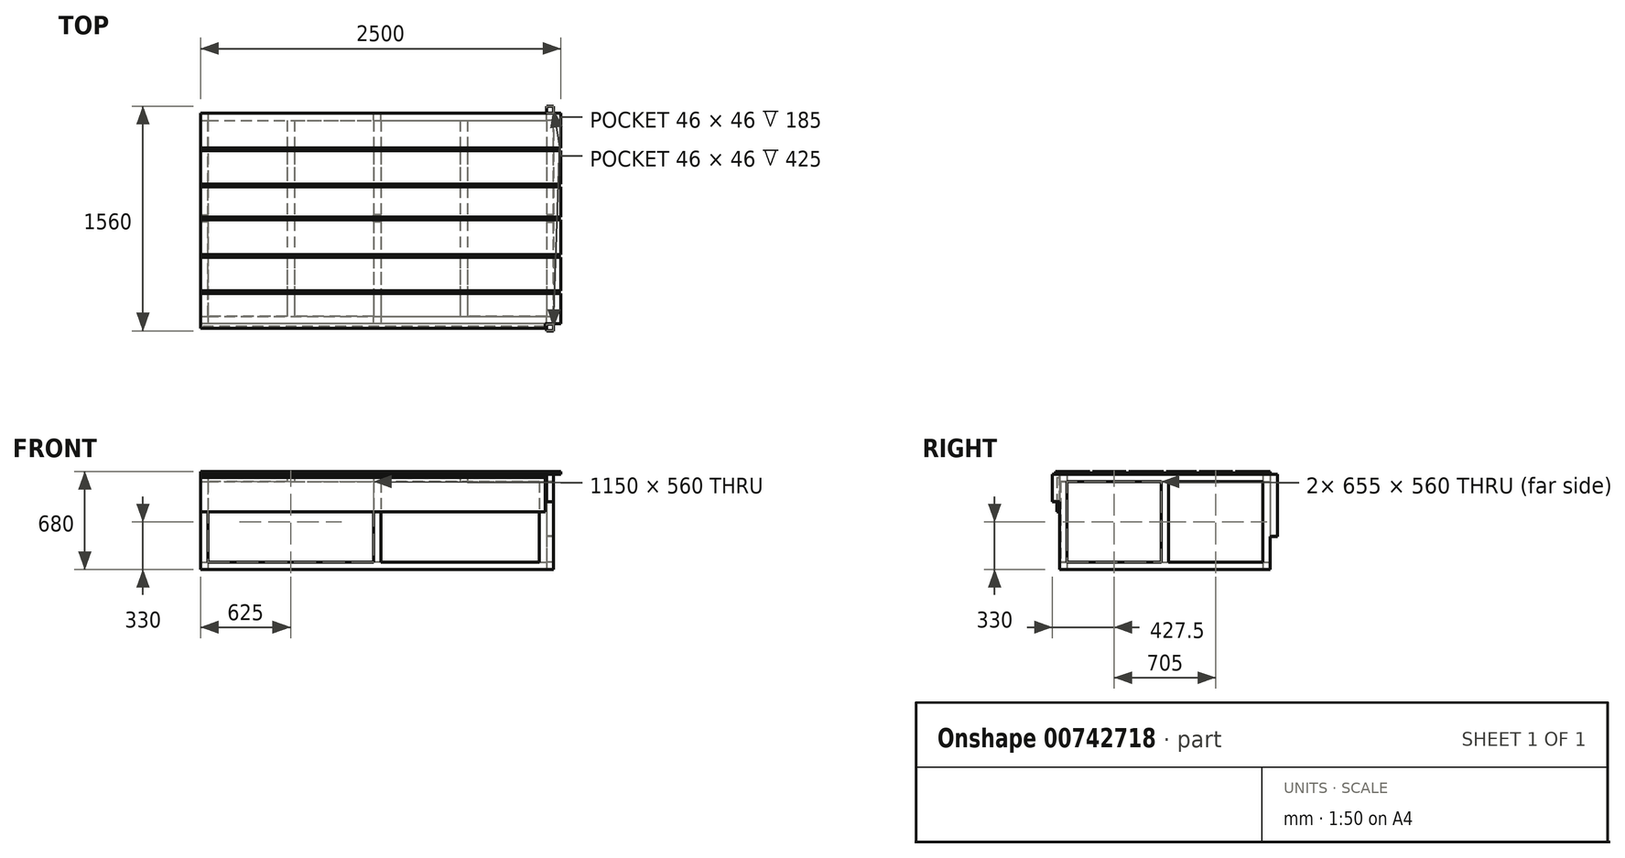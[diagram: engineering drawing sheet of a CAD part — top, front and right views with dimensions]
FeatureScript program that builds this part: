
annotation { "Feature Type Name" : "Feature", "Feature Type Description" : "" }
export const myFeature = defineFeature(function(context is Context, id is Id, definition is map)
    precondition{}
    {
        {
            var Q0;
            Q0=qCreatedBy(makeId("Top.planeOp"),FACE);
            var sketch = newSketch(context, id + "F0", { "sketchPlane" : qUnion([Q0])});
            skLineSegment(sketch, "E0.bottom", {"start": v(1225, -730) * mm, "end": v(-1225, -730) * mm});
            skLineSegment(sketch, "E0.top", {"start": v(1225, 730) * mm, "end": v(-1225, 730) * mm});
            skLineSegment(sketch, "E0.left", {"start": v(1225, -730) * mm, "end": v(1225, 730) * mm});
            skLineSegment(sketch, "E0.right", {"start": v(-1225, -730) * mm, "end": v(-1225, 730) * mm});
            skPoint(sketch, "E0.middle", {"position": v(0, 0) * mm});
            skLineSegment(sketch, "E1.bottom", {"start": v(-1175, 680) * mm, "end": v(1175, 680) * mm});
            skLineSegment(sketch, "E1.top", {"start": v(-1175, -680) * mm, "end": v(1175, -680) * mm});
            skLineSegment(sketch, "E1.left", {"start": v(-1175, 680) * mm, "end": v(-1175, -680) * mm});
            skLineSegment(sketch, "E1.right", {"start": v(1175, 680) * mm, "end": v(1175, -680) * mm});
            skLineSegment(sketch, "E2.bottom", {"start": v(25, 680) * mm, "end": v(-25, 680) * mm});
            skLineSegment(sketch, "E2.top", {"start": v(25, -680) * mm, "end": v(-25, -680) * mm});
            skLineSegment(sketch, "E2.left", {"start": v(25, 680) * mm, "end": v(25, -680) * mm});
            skLineSegment(sketch, "E2.right", {"start": v(-25, 680) * mm, "end": v(-25, -680) * mm});
            skSolve(sketch);
        }
        {
            var Q0;
            Q0=qSketchRegion(id+"F0",true);
            var Q1;
            Q1=makeQuery(id+"F0.imprint","IMPRINT",FACE,{"disambiguationData":[TD([[makeQuery(id+"F0.imprint","IMPRINT",EDGE,{"derivedFrom":sQuery(id+"F0.wireOp",EDGE,"E2.bottom")}),1.0]])]});
            extrude(context, id + "F1", {"entities" : qUnion([Q0, Q1]), "depth" : 50 * mm, "offsetDistance" : 25 * mm});
        }
        {
            var Q0;
            Q0=makeQuery(id+"F1.opExtrude","CAP_FACE",FACE,{"disambiguationData":[OSD([sQuery(id+"F0.wireOp",EDGE,"E0.bottom"),sQuery(id+"F0.wireOp",EDGE,"E0.top"),sQuery(id+"F0.wireOp",EDGE,"E0.left"),sQuery(id+"F0.wireOp",EDGE,"E0.right"),sQuery(id+"F0.wireOp",EDGE,"E1.bottom"),sQuery(id+"F0.wireOp",EDGE,"E1.top"),sQuery(id+"F0.wireOp",EDGE,"E1.left"),sQuery(id+"F0.wireOp",EDGE,"E1.right"),sQuery(id+"F0.wireOp",EDGE,"E2.left"),sQuery(id+"F0.wireOp",EDGE,"E2.right")])],"isStart":false});
            var sketch = newSketch(context, id + "F2", { "sketchPlane" : qUnion([Q0])});
            skLineSegment(sketch, "E3.bottom", {"start": v(-1225, 730) * mm, "end": v(-1175, 730) * mm});
            skLineSegment(sketch, "E3.top", {"start": v(-1225, 680) * mm, "end": v(-1175, 680) * mm});
            skLineSegment(sketch, "E3.left", {"start": v(-1225, 730) * mm, "end": v(-1225, 680) * mm});
            skLineSegment(sketch, "E3.right", {"start": v(-1175, 730) * mm, "end": v(-1175, 680) * mm});
            skLineSegment(sketch, "E4", {"start": v(-25, 680) * mm, "end": v(-25, 730) * mm});
            skLineSegment(sketch, "E5", {"start": v(25, 680) * mm, "end": v(25, 730) * mm});
            skLineSegment(sketch, "E6", {"start": v(25, 730) * mm, "end": v(-25, 730) * mm});
            skLineSegment(sketch, "E7", {"start": v(-25, 680) * mm, "end": v(25, 680) * mm});
            skLineSegment(sketch, "E8", {"start": v(1175, 680) * mm, "end": v(1175, 730) * mm});
            skLineSegment(sketch, "E9", {"start": v(1175, 730) * mm, "end": v(1225, 730) * mm});
            skLineSegment(sketch, "E10", {"start": v(1225, 730) * mm, "end": v(1225, 680) * mm});
            skLineSegment(sketch, "E11", {"start": v(1225, 680) * mm, "end": v(1175, 680) * mm});
            skLineSegment(sketch, "E12", {"start": v(1175, -680) * mm, "end": v(1225, -680) * mm});
            skLineSegment(sketch, "E13", {"start": v(1225, -680) * mm, "end": v(1225, -730) * mm});
            skLineSegment(sketch, "E14", {"start": v(1225, -730) * mm, "end": v(1175, -730) * mm});
            skLineSegment(sketch, "E15", {"start": v(1175, -730) * mm, "end": v(1175, -680) * mm});
            skLineSegment(sketch, "E16", {"start": v(-25, -680) * mm, "end": v(25, -680) * mm});
            skLineSegment(sketch, "E17", {"start": v(25, -680) * mm, "end": v(25, -730) * mm});
            skLineSegment(sketch, "E18", {"start": v(25, -730) * mm, "end": v(-25, -730) * mm});
            skLineSegment(sketch, "E19", {"start": v(-25, -730) * mm, "end": v(-25, -680) * mm});
            skLineSegment(sketch, "E20", {"start": v(-1175, -680) * mm, "end": v(-1175, -730) * mm});
            skLineSegment(sketch, "E21", {"start": v(-1175, -730) * mm, "end": v(-1225, -730) * mm});
            skLineSegment(sketch, "E22", {"start": v(-1225, -730) * mm, "end": v(-1225, -680) * mm});
            skLineSegment(sketch, "E23", {"start": v(-1225, -680) * mm, "end": v(-1175, -680) * mm});
            skLineSegment(sketch, "E24.bottom", {"start": v(25, -25) * mm, "end": v(-25, -25) * mm});
            skLineSegment(sketch, "E24.top", {"start": v(25, 25) * mm, "end": v(-25, 25) * mm});
            skLineSegment(sketch, "E24.left", {"start": v(25, -25) * mm, "end": v(25, 25) * mm});
            skLineSegment(sketch, "E24.right", {"start": v(-25, -25) * mm, "end": v(-25, 25) * mm});
            skPoint(sketch, "E24.middle", {"position": v(0, 0) * mm});
            skLineSegment(sketch, "E25", {"start": v(0, 0) * mm, "end": v(-1225, 0) * mm});
            skLineSegment(sketch, "E26", {"start": v(-1225, 25) * mm, "end": v(-1175, 25) * mm});
            skLineSegment(sketch, "E27", {"start": v(-1175, 25) * mm, "end": v(-1175, -25) * mm});
            skLineSegment(sketch, "E28", {"start": v(-1175, -25) * mm, "end": v(-1225, -25) * mm});
            skLineSegment(sketch, "E29", {"start": v(-1225, 25) * mm, "end": v(-1225, -25) * mm});
            skLineSegment(sketch, "E30.MirrorCS", {"start": v(1225, 25) * mm, "end": v(1225, -25) * mm});
            skLineSegment(sketch, "E31.MirrorCS", {"start": v(1175, -25) * mm, "end": v(1225, -25) * mm});
            skLineSegment(sketch, "E32.MirrorCS", {"start": v(1225, 25) * mm, "end": v(1175, 25) * mm});
            skLineSegment(sketch, "E33.MirrorCS", {"start": v(1175, 25) * mm, "end": v(1175, -25) * mm});
            skSolve(sketch);
        }
        {
            var Q0;
            Q0=qSketchRegion(id+"F2",true);
            extrude(context, id + "F3", {"entities" : qUnion([Q0]), "operationType" : NewBodyOperationType.ADD, "depth" : 560 * mm, "offsetDistance" : 25 * mm});
        }
        {
            var Q0;
            Q0=makeQuery(id+"F3.opExtrude","CAP_FACE",FACE,{"disambiguationData":[OSD([sQuery(id+"F2.wireOp",EDGE,"E26"),sQuery(id+"F2.wireOp",EDGE,"E27"),sQuery(id+"F2.wireOp",EDGE,"E28"),sQuery(id+"F2.wireOp",EDGE,"E29")])],"isStart":false});
            var sketch = newSketch(context, id + "F4", { "sketchPlane" : qUnion([Q0])});
            skLineSegment(sketch, "E34", {"start": v(-1225, 25) * mm, "end": v(-1225, 730) * mm});
            skLineSegment(sketch, "E35", {"start": v(-1225, 730) * mm, "end": v(-1175, 730) * mm});
            skLineSegment(sketch, "E36", {"start": v(-1175, 730) * mm, "end": v(1225, 730) * mm});
            skLineSegment(sketch, "E37", {"start": v(1225, 730) * mm, "end": v(1225, -730) * mm});
            skLineSegment(sketch, "E38", {"start": v(1225, -730) * mm, "end": v(-1225, -730) * mm});
            skLineSegment(sketch, "E39", {"start": v(-1225, -730) * mm, "end": v(-1225, 25) * mm});
            skLineSegment(sketch, "E40", {"start": v(-1175, 730) * mm, "end": v(-1175, 680) * mm});
            skLineSegment(sketch, "E41", {"start": v(-1175, 680) * mm, "end": v(-25, 680) * mm});
            skLineSegment(sketch, "E42", {"start": v(-1175, 680) * mm, "end": v(-600, 680) * mm});
            skLineSegment(sketch, "E43", {"start": v(-600, 680) * mm, "end": v(-575, 680) * mm});
            skLineSegment(sketch, "E44", {"start": v(-600, 680) * mm, "end": v(-625, 680) * mm});
            skLineSegment(sketch, "E45", {"start": v(-625, 680) * mm, "end": v(-625, -680) * mm});
            skLineSegment(sketch, "E46.MirrorCS", {"start": v(-575, 680) * mm, "end": v(-575, -680) * mm});
            skLineSegment(sketch, "E47", {"start": v(-25, 680) * mm, "end": v(25, 680) * mm});
            skLineSegment(sketch, "E48", {"start": v(25, 680) * mm, "end": v(1175, 680) * mm});
            skLineSegment(sketch, "E49", {"start": v(25, 680) * mm, "end": v(600, 680) * mm});
            skLineSegment(sketch, "E50", {"start": v(600, 680) * mm, "end": v(575, 680) * mm});
            skLineSegment(sketch, "E51", {"start": v(575, 680) * mm, "end": v(575, -680) * mm});
            skLineSegment(sketch, "E52.MirrorCS", {"start": v(625, 680) * mm, "end": v(625, -680) * mm});
            skLineSegment(sketch, "E53", {"start": v(-25, 680) * mm, "end": v(-25, -680) * mm});
            skLineSegment(sketch, "E54", {"start": v(-25, -680) * mm, "end": v(-575, -680) * mm});
            skLineSegment(sketch, "E55", {"start": v(-625, -680) * mm, "end": v(-1175, -680) * mm});
            skLineSegment(sketch, "E56", {"start": v(-1175, -680) * mm, "end": v(-1175, 680) * mm});
            skLineSegment(sketch, "E57", {"start": v(1175, 680) * mm, "end": v(1175, -680) * mm});
            skLineSegment(sketch, "E58", {"start": v(1175, -680) * mm, "end": v(625, -680) * mm});
            skLineSegment(sketch, "E59", {"start": v(25, 680) * mm, "end": v(25, -680) * mm});
            skLineSegment(sketch, "E60", {"start": v(25, -680) * mm, "end": v(575, -680) * mm});
            skSolve(sketch);
        }
        {
            var Q0;
            Q0=qSketchRegion(id+"F4",true);
            extrude(context, id + "F5", {"entities" : qUnion([Q0]), "operationType" : NewBodyOperationType.ADD, "depth" : 50 * mm, "offsetDistance" : 25 * mm});
        }
        {
            var Q0;
            {var subQ5=sQuery(id+"F0.wireOp",EDGE,"E1.left");var subQ6=sQuery(id+"F0.wireOp",EDGE,"E1.top");var subQ8=makeQuery(id+"F1.opExtrude","CAP_EDGE",EDGE,{"disambiguationData":[OSD([subQ6]),TDD([makeQuery(id+"F0.imprint","IMPRINT",EDGE,{"disambiguationData":[TD([[makeQuery(id+"F0.imprint","INTERSECT",VERTEX,{"derivedFrom":[subQ6,subQ5]}),-1.0]])],"derivedFrom":subQ6})])],"isStart":false});Q0=makeQuery(id+"F2.imprint","IMPRINT",FACE,{"disambiguationData":[TD([[makeQuery(id+"F2.imprint","IMPRINT",EDGE,{"derivedFrom":subQ8}),1.0]])]});}
            cPlane(context, id + "F6", {"entities" : qUnion([Q0]), "cplaneType" : CPlaneType.OFFSET, "offset" : 420 * mm, "width" : 150 * mm, "height" : 150 * mm});
        }
        {
            var Q0;
            {var subQ5=sQuery(id+"F0.wireOp",EDGE,"E1.left");var subQ6=sQuery(id+"F0.wireOp",EDGE,"E1.top");var subQ8=makeQuery(id+"F1.opExtrude","CAP_EDGE",EDGE,{"disambiguationData":[OSD([subQ6]),TDD([makeQuery(id+"F0.imprint","IMPRINT",EDGE,{"disambiguationData":[TD([[makeQuery(id+"F0.imprint","INTERSECT",VERTEX,{"derivedFrom":[subQ6,subQ5]}),-1.0]])],"derivedFrom":subQ6})])],"isStart":false});Q0=makeQuery(id+"F2.imprint","IMPRINT",FACE,{"disambiguationData":[TD([[makeQuery(id+"F2.imprint","IMPRINT",EDGE,{"derivedFrom":subQ8}),1.0]])]});}
            cPlane(context, id + "F7", {"entities" : qUnion([Q0]), "cplaneType" : CPlaneType.OFFSET, "offset" : 180 * mm, "width" : 150 * mm, "height" : 150 * mm});
        }
        {
            var Q0;
            Q0=qCreatedBy(id+"F7.planeOp",FACE);
            var sketch = newSketch(context, id + "F8", { "sketchPlane" : qUnion([Q0])});
            skLineSegment(sketch, "E61.bottom", {"start": v(1225, 730) * mm, "end": v(1175, 730) * mm});
            skLineSegment(sketch, "E61.top", {"start": v(1225, 780) * mm, "end": v(1175, 780) * mm});
            skLineSegment(sketch, "E61.left", {"start": v(1225, 730) * mm, "end": v(1225, 780) * mm});
            skLineSegment(sketch, "E61.right", {"start": v(1175, 730) * mm, "end": v(1175, 780) * mm});
            skSolve(sketch);
        }
        {
            var Q0;
            Q0=qCreatedBy(id+"F6.planeOp",FACE);
            var sketch = newSketch(context, id + "F9", { "sketchPlane" : qUnion([Q0])});
            skLineSegment(sketch, "E62.bottom", {"start": v(1225, -730) * mm, "end": v(1175, -730) * mm});
            skLineSegment(sketch, "E62.top", {"start": v(1225, -780) * mm, "end": v(1175, -780) * mm});
            skLineSegment(sketch, "E62.right", {"start": v(1175, -730) * mm, "end": v(1175, -780) * mm});
            skLineSegment(sketch, "E63", {"start": v(1225, -730) * mm, "end": v(1225, -780) * mm});
            skSolve(sketch);
        }
        {
            var Q0;
            Q0 = qSketchRegion(id + "F9", true);
            extrude(context, id + "F10", {"entities" : qUnion([Q0]), "operationType" : NewBodyOperationType.ADD, "depth" : 5 * mm, "offsetDistance" : 25 * mm});
        }
        {
            var Q0;
            Q0=makeQuery(id+"F10.opExtrude","CAP_FACE",FACE,{"disambiguationData":[OSD([sQuery(id+"F9.wireOp",EDGE,"E62.bottom"),sQuery(id+"F9.wireOp",EDGE,"E62.top"),sQuery(id+"F9.wireOp",EDGE,"E62.right"),sQuery(id+"F9.wireOp",EDGE,"E63")])],"isStart":false});
            var sketch = newSketch(context, id + "F11", { "sketchPlane" : qUnion([Q0])});
            skLineSegment(sketch, "E64", {"start": v(1175, -730) * mm, "end": v(1175, -780) * mm});
            skLineSegment(sketch, "E65", {"start": v(1175, -780) * mm, "end": v(1225, -780) * mm});
            skLineSegment(sketch, "E66", {"start": v(1225, -780) * mm, "end": v(1225, -730) * mm});
            skLineSegment(sketch, "E67", {"start": v(1225, -730) * mm, "end": v(1175, -730) * mm});
            skLineSegment(sketch, "E68", {"start": v(1175, -730) * mm, "end": v(1177, -730) * mm});
            skLineSegment(sketch, "E69", {"start": v(1177, -730) * mm, "end": v(1177, -732) * mm});
            skLineSegment(sketch, "E70.bottom", {"start": v(1177, -732) * mm, "end": v(1223, -732) * mm});
            skLineSegment(sketch, "E70.top", {"start": v(1177, -778) * mm, "end": v(1223, -778) * mm});
            skLineSegment(sketch, "E70.left", {"start": v(1177, -732) * mm, "end": v(1177, -778) * mm});
            skLineSegment(sketch, "E70.right", {"start": v(1223, -732) * mm, "end": v(1223, -778) * mm});
            skSolve(sketch);
        }
        {
            var Q0;
            Q0 = qSketchRegion(id + "F11", true);
            var Q1;
            {var subQ0=sQuery(id+"F4.wireOp",EDGE,"E60");var subQ1=sQuery(id+"F4.wireOp",EDGE,"E59");var subQ2=sQuery(id+"F4.wireOp",EDGE,"E58");var subQ3=sQuery(id+"F4.wireOp",EDGE,"E57");var subQ4=sQuery(id+"F4.wireOp",EDGE,"E56");var subQ5=sQuery(id+"F4.wireOp",EDGE,"E55");var subQ6=sQuery(id+"F4.wireOp",EDGE,"E54");var subQ7=sQuery(id+"F4.wireOp",EDGE,"E53");var subQ8=sQuery(id+"F4.wireOp",EDGE,"E52.MirrorCS");var subQ9=sQuery(id+"F4.wireOp",EDGE,"E51");var subQ10=sQuery(id+"F4.wireOp",EDGE,"E49");var subQ11=sQuery(id+"F4.wireOp",EDGE,"E48");var subQ12=sQuery(id+"F4.wireOp",EDGE,"E46.MirrorCS");var subQ13=sQuery(id+"F4.wireOp",EDGE,"E45");var subQ14=sQuery(id+"F4.wireOp",EDGE,"E42");var subQ15=sQuery(id+"F4.wireOp",EDGE,"E41");var subQ16=sQuery(id+"F4.wireOp",EDGE,"E39");var subQ17=sQuery(id+"F4.wireOp",EDGE,"E38");var subQ18=sQuery(id+"F4.wireOp",EDGE,"E37");var subQ19=sQuery(id+"F4.wireOp",EDGE,"E36");var subQ20=sQuery(id+"F4.wireOp",EDGE,"E35");var subQ21=sQuery(id+"F4.wireOp",EDGE,"E34");Q1=makeQuery(id+"FP4IzDu3Lu8PIDH_1.boolean.opBoolean","MERGE",FACE,{"derivedFrom":[makeQuery(id+"F5.opExtrude","CAP_FACE",FACE,{"disambiguationData":[OSD([subQ21,subQ20,subQ19,subQ18,subQ17,subQ16,subQ15,subQ14,subQ13,subQ12,subQ11,subQ10,subQ9,subQ8,subQ7,subQ6,subQ5,subQ4,subQ3,subQ2,subQ1,subQ0])],"isStart":false}),makeQuery(id+"FP4IzDu3Lu8PIDH_1.opExtrude","CAP_FACE",FACE,{"disambiguationData":[OSD([subQ21,subQ20,subQ19,subQ18,subQ17,subQ16,subQ15,subQ14,subQ13,subQ12,subQ11,subQ10,subQ9,subQ8,subQ7,subQ6,subQ5,subQ4,subQ3,subQ2,subQ1,subQ0])],"isStart":false})]});}
            extrude(context, id + "F12", {"entities" : qUnion([Q0]), "operationType" : NewBodyOperationType.ADD, "endBound" : BoundingType.UP_TO_SURFACE, "depth" : 25 * mm, "endBoundEntityFace" : qUnion([Q1]), "offsetDistance" : 25 * mm});
        }
        {
            var Q0;
            Q0 = qSketchRegion(id + "F8", true);
            extrude(context, id + "F13", {"entities" : qUnion([Q0]), "operationType" : NewBodyOperationType.ADD, "depth" : 5 * mm, "offsetDistance" : 25 * mm});
        }
        {
            var Q0;
            Q0=makeQuery(id+"F13.opExtrude","CAP_FACE",FACE,{"disambiguationData":[OSD([sQuery(id+"F8.wireOp",EDGE,"E61.bottom"),sQuery(id+"F8.wireOp",EDGE,"E61.top"),sQuery(id+"F8.wireOp",EDGE,"E61.left"),sQuery(id+"F8.wireOp",EDGE,"E61.right")])],"isStart":false});
            var sketch = newSketch(context, id + "F14", { "sketchPlane" : qUnion([Q0])});
            skLineSegment(sketch, "E71.bottom", {"start": v(1175, 780) * mm, "end": v(1177, 780) * mm});
            skLineSegment(sketch, "E71.top", {"start": v(1175, 778) * mm, "end": v(1177, 778) * mm});
            skLineSegment(sketch, "E71.left", {"start": v(1175, 780) * mm, "end": v(1175, 778) * mm});
            skLineSegment(sketch, "E71.right", {"start": v(1177, 780) * mm, "end": v(1177, 778) * mm});
            skLineSegment(sketch, "E72.bottom", {"start": v(1177, 778) * mm, "end": v(1223, 778) * mm});
            skLineSegment(sketch, "E72.top", {"start": v(1177, 732) * mm, "end": v(1223, 732) * mm});
            skLineSegment(sketch, "E72.left", {"start": v(1177, 778) * mm, "end": v(1177, 732) * mm});
            skLineSegment(sketch, "E72.right", {"start": v(1223, 778) * mm, "end": v(1223, 732) * mm});
            skLineSegment(sketch, "E73.bottom", {"start": v(1175, 780) * mm, "end": v(1225, 780) * mm});
            skLineSegment(sketch, "E73.top", {"start": v(1175, 730) * mm, "end": v(1225, 730) * mm});
            skLineSegment(sketch, "E73.left", {"start": v(1175, 780) * mm, "end": v(1175, 730) * mm});
            skLineSegment(sketch, "E73.right", {"start": v(1225, 780) * mm, "end": v(1225, 730) * mm});
            skSolve(sketch);
        }
        {
            var Q0;
            Q0 = qSketchRegion(id + "F14", true);
            var Q1;
            {var subQ0=sQuery(id+"F4.wireOp",EDGE,"E60");var subQ1=sQuery(id+"F4.wireOp",EDGE,"E59");var subQ2=sQuery(id+"F4.wireOp",EDGE,"E58");var subQ3=sQuery(id+"F4.wireOp",EDGE,"E57");var subQ4=sQuery(id+"F4.wireOp",EDGE,"E56");var subQ5=sQuery(id+"F4.wireOp",EDGE,"E55");var subQ6=sQuery(id+"F4.wireOp",EDGE,"E54");var subQ7=sQuery(id+"F4.wireOp",EDGE,"E53");var subQ8=sQuery(id+"F4.wireOp",EDGE,"E52.MirrorCS");var subQ9=sQuery(id+"F4.wireOp",EDGE,"E51");var subQ10=sQuery(id+"F4.wireOp",EDGE,"E49");var subQ11=sQuery(id+"F4.wireOp",EDGE,"E48");var subQ12=sQuery(id+"F4.wireOp",EDGE,"E46.MirrorCS");var subQ13=sQuery(id+"F4.wireOp",EDGE,"E45");var subQ14=sQuery(id+"F4.wireOp",EDGE,"E42");var subQ15=sQuery(id+"F4.wireOp",EDGE,"E41");var subQ16=sQuery(id+"F4.wireOp",EDGE,"E39");var subQ17=sQuery(id+"F4.wireOp",EDGE,"E38");var subQ18=sQuery(id+"F4.wireOp",EDGE,"E37");var subQ19=sQuery(id+"F4.wireOp",EDGE,"E36");var subQ20=sQuery(id+"F4.wireOp",EDGE,"E35");var subQ21=sQuery(id+"F4.wireOp",EDGE,"E34");Q1=makeQuery(id+"F12.boolean.opBoolean","MERGE",FACE,{"derivedFrom":[makeQuery(id+"F5.opExtrude","CAP_FACE",FACE,{"disambiguationData":[OSD([subQ21,subQ20,subQ19,subQ18,subQ17,subQ16,subQ15,subQ14,subQ13,subQ12,subQ11,subQ10,subQ9,subQ8,subQ7,subQ6,subQ5,subQ4,subQ3,subQ2,subQ1,subQ0])],"isStart":false}),makeQuery(id+"F12.opExtrude","CAP_FACE",FACE,{"disambiguationData":[OSD([subQ21,subQ20,subQ19,subQ18,subQ17,subQ16,subQ15,subQ14,subQ13,subQ12,subQ11,subQ10,subQ9,subQ8,subQ7,subQ6,subQ5,subQ4,subQ3,subQ2,subQ1,subQ0])],"isStart":false})]});}
            extrude(context, id + "F15", {"entities" : qUnion([Q0]), "operationType" : NewBodyOperationType.ADD, "endBound" : BoundingType.UP_TO_SURFACE, "depth" : 25 * mm, "endBoundEntityFace" : qUnion([Q1]), "offsetDistance" : 25 * mm});
        }
        {
            var Q0;
            {var subQ0=sQuery(id+"F4.wireOp",EDGE,"E60");var subQ1=sQuery(id+"F4.wireOp",EDGE,"E59");var subQ2=sQuery(id+"F4.wireOp",EDGE,"E58");var subQ3=sQuery(id+"F4.wireOp",EDGE,"E57");var subQ4=sQuery(id+"F4.wireOp",EDGE,"E56");var subQ5=sQuery(id+"F4.wireOp",EDGE,"E55");var subQ6=sQuery(id+"F4.wireOp",EDGE,"E54");var subQ7=sQuery(id+"F4.wireOp",EDGE,"E53");var subQ8=sQuery(id+"F4.wireOp",EDGE,"E52.MirrorCS");var subQ9=sQuery(id+"F4.wireOp",EDGE,"E51");var subQ10=sQuery(id+"F4.wireOp",EDGE,"E49");var subQ11=sQuery(id+"F4.wireOp",EDGE,"E48");var subQ12=sQuery(id+"F4.wireOp",EDGE,"E46.MirrorCS");var subQ13=sQuery(id+"F4.wireOp",EDGE,"E45");var subQ14=sQuery(id+"F4.wireOp",EDGE,"E42");var subQ15=sQuery(id+"F4.wireOp",EDGE,"E41");var subQ16=sQuery(id+"F4.wireOp",EDGE,"E39");var subQ17=sQuery(id+"F4.wireOp",EDGE,"E38");var subQ18=sQuery(id+"F4.wireOp",EDGE,"E37");var subQ19=sQuery(id+"F4.wireOp",EDGE,"E36");var subQ20=sQuery(id+"F4.wireOp",EDGE,"E35");var subQ21=sQuery(id+"F4.wireOp",EDGE,"E34");Q0=makeQuery(id+"F15.boolean.opBoolean","MERGE",FACE,{"derivedFrom":[makeQuery(id+"F12.boolean.opBoolean","MERGE",FACE,{"derivedFrom":[makeQuery(id+"F5.opExtrude","CAP_FACE",FACE,{"disambiguationData":[OSD([subQ21,subQ20,subQ19,subQ18,subQ17,subQ16,subQ15,subQ14,subQ13,subQ12,subQ11,subQ10,subQ9,subQ8,subQ7,subQ6,subQ5,subQ4,subQ3,subQ2,subQ1,subQ0])],"isStart":false}),makeQuery(id+"F12.opExtrude","CAP_FACE",FACE,{"disambiguationData":[OSD([subQ21,subQ20,subQ19,subQ18,subQ17,subQ16,subQ15,subQ14,subQ13,subQ12,subQ11,subQ10,subQ9,subQ8,subQ7,subQ6,subQ5,subQ4,subQ3,subQ2,subQ1,subQ0])],"isStart":false})]}),makeQuery(id+"F15.opExtrude","CAP_FACE",FACE,{"disambiguationData":[OSD([subQ21,subQ20,subQ19,subQ18,subQ17,subQ16,subQ15,subQ14,subQ13,subQ12,subQ11,subQ10,subQ9,subQ8,subQ7,subQ6,subQ5,subQ4,subQ3,subQ2,subQ1,subQ0])],"isStart":false})]});}
            var sketch = newSketch(context, id + "F16", { "sketchPlane" : qUnion([Q0])});
            skLineSegment(sketch, "E74.bottom", {"start": v(-1225, 730) * mm, "end": v(1225, 730) * mm});
            skLineSegment(sketch, "E74.top", {"start": v(-1225, -730) * mm, "end": v(1225, -730) * mm});
            skLineSegment(sketch, "E74.left", {"start": v(-1225, 730) * mm, "end": v(-1225, -730) * mm});
            skLineSegment(sketch, "E74.right", {"start": v(1225, 730) * mm, "end": v(1225, -730) * mm});
            skLineSegment(sketch, "E75", {"start": v(1175, -730) * mm, "end": v(1165, -730) * mm});
            skLineSegment(sketch, "E76.bottom", {"start": v(1165, -730) * mm, "end": v(-1225, -730) * mm});
            skLineSegment(sketch, "E76.top", {"start": v(1165, -760) * mm, "end": v(-1225, -760) * mm});
            skLineSegment(sketch, "E76.left", {"start": v(1165, -730) * mm, "end": v(1165, -760) * mm});
            skLineSegment(sketch, "E76.right", {"start": v(-1225, -730) * mm, "end": v(-1225, -760) * mm});
            skLineSegment(sketch, "E77.bottom", {"start": v(1225, -730) * mm, "end": v(1275, -730) * mm});
            skLineSegment(sketch, "E77.top", {"start": v(1225, 730) * mm, "end": v(1275, 730) * mm});
            skLineSegment(sketch, "E77.left", {"start": v(1225, -730) * mm, "end": v(1225, 730) * mm});
            skLineSegment(sketch, "E77.right", {"start": v(1275, -730) * mm, "end": v(1275, 730) * mm});
            skSolve(sketch);
        }
        {
            var Q0;
            Q0 = qSketchRegion(id + "F16", true);
            extrude(context, id + "F17", {"entities" : qUnion([Q0]), "depth" : 20 * mm, "offsetDistance" : 25 * mm});
        }
        {
            var Q0;
            Q0=makeQuery(id+"F12.boolean.opBoolean","MERGE",FACE,{"derivedFrom":[makeQuery(id+"F10.boolean.opBoolean","MERGE",FACE,{"derivedFrom":[makeQuery(id+"F3.opExtrude","SWEPT_FACE",FACE,{"disambiguationData":[OSD([sQuery(id+"F2.wireOp",EDGE,"E15")])]}),makeQuery(id+"F10.opExtrude","SWEPT_FACE",FACE,{"disambiguationData":[OSD([sQuery(id+"F9.wireOp",EDGE,"E62.right")])]})]}),makeQuery(id+"F12.opExtrude","SWEPT_FACE",FACE,{"disambiguationData":[OSD([sQuery(id+"F11.wireOp",EDGE,"E64")])]})]});
            var sketch = newSketch(context, id + "F18", { "sketchPlane" : qUnion([Q0])});
            skLineSegment(sketch, "E78.bottom", {"start": v(730, 610) * mm, "end": v(725, 610) * mm});
            skLineSegment(sketch, "E78.top", {"start": v(730, 50) * mm, "end": v(725, 50) * mm});
            skLineSegment(sketch, "E78.left", {"start": v(730, 610) * mm, "end": v(730, 50) * mm});
            skLineSegment(sketch, "E78.right", {"start": v(725, 610) * mm, "end": v(725, 50) * mm});
            skSolve(sketch);
        }
        {
            var Q0;
            Q0 = qSketchRegion(id + "F18", true);
            extrude(context, id + "F19", {"entities" : qUnion([Q0]), "operationType" : NewBodyOperationType.ADD, "depth" : 50 * mm, "offsetDistance" : 25 * mm});
        }
        {
            var Q0;
            Q0=makeQuery(id+"F19.boolean.opBoolean","MERGE",FACE,{"derivedFrom":[makeQuery(id+"F5.boolean.opBoolean","MERGE",FACE,{"derivedFrom":[makeQuery(id+"F3.boolean.opBoolean","MERGE",FACE,{"derivedFrom":[makeQuery(id+"F1.opExtrude","SWEPT_FACE",FACE,{"disambiguationData":[OSD([sQuery(id+"F0.wireOp",EDGE,"E0.bottom")])]}),makeQuery(id+"F3.opExtrude","SWEPT_FACE",FACE,{"disambiguationData":[OSD([sQuery(id+"F2.wireOp",EDGE,"E14")])]}),makeQuery(id+"F3.opExtrude","SWEPT_FACE",FACE,{"disambiguationData":[OSD([sQuery(id+"F2.wireOp",EDGE,"E18")])]}),makeQuery(id+"F3.opExtrude","SWEPT_FACE",FACE,{"disambiguationData":[OSD([sQuery(id+"F2.wireOp",EDGE,"E21")])]})]}),makeQuery(id+"F5.opExtrude","SWEPT_FACE",FACE,{"disambiguationData":[OSD([sQuery(id+"F4.wireOp",EDGE,"E38")])]})]}),makeQuery(id+"F19.opExtrude","SWEPT_FACE",FACE,{"disambiguationData":[OSD([sQuery(id+"F18.wireOp",EDGE,"E78.left")])]})]});
            var sketch = newSketch(context, id + "F20", { "sketchPlane" : qUnion([Q0])});
            skLineSegment(sketch, "E79", {"start": v(1225, 660) * mm, "end": v(1225, 640) * mm});
            skLineSegment(sketch, "E80", {"start": v(1225, 640) * mm, "end": v(1165, 640) * mm});
            skLineSegment(sketch, "E81.bottom", {"start": v(1165, 640) * mm, "end": v(-1225, 640) * mm});
            skLineSegment(sketch, "E81.top", {"start": v(1165, 400) * mm, "end": v(-1225, 400) * mm});
            skLineSegment(sketch, "E81.left", {"start": v(1165, 640) * mm, "end": v(1165, 400) * mm});
            skLineSegment(sketch, "E81.right", {"start": v(-1225, 640) * mm, "end": v(-1225, 400) * mm});
            skSolve(sketch);
        }
        {
            var Q0;
            Q0 = qSketchRegion(id + "F20", true);
            extrude(context, id + "F21", {"entities" : qUnion([Q0]), "depth" : 20 * mm, "offsetDistance" : 25 * mm});
        }
        {
            var Q0;
            Q0=makeQuery(id+"F17.opExtrude","SWEPT_FACE",FACE,{"disambiguationData":[OSD([sQuery(id+"F16.wireOp",EDGE,"E74.left"),sQuery(id+"F16.wireOp",EDGE,"E76.right")])]});
            var sketch = newSketch(context, id + "F22", { "sketchPlane" : qUnion([Q0])});
            skLineSegment(sketch, "E82", {"start": v(730, 680) * mm, "end": v(10, 680) * mm});
            skLineSegment(sketch, "E83.bottom", {"start": v(10, 680) * mm, "end": v(-10, 680) * mm});
            skLineSegment(sketch, "E83.top", {"start": v(10, 660) * mm, "end": v(-10, 660) * mm});
            skLineSegment(sketch, "E83.left", {"start": v(10, 680) * mm, "end": v(10, 660) * mm});
            skLineSegment(sketch, "E83.right", {"start": v(-10, 680) * mm, "end": v(-10, 660) * mm});
            skLineSegment(sketch, "E84", {"start": v(-10, 680) * mm, "end": v(-160.18, 680) * mm});
            skLineSegment(sketch, "E85", {"start": v(730, 680) * mm, "end": v(520, 680) * mm});
            skLineSegment(sketch, "E86.bottom", {"start": v(520, 680) * mm, "end": v(500, 680) * mm});
            skLineSegment(sketch, "E86.top", {"start": v(520, 660) * mm, "end": v(500, 660) * mm});
            skLineSegment(sketch, "E86.left", {"start": v(520, 680) * mm, "end": v(520, 660) * mm});
            skLineSegment(sketch, "E86.right", {"start": v(500, 680) * mm, "end": v(500, 660) * mm});
            skLineSegment(sketch, "E87", {"start": v(500, 680) * mm, "end": v(270, 680) * mm});
            skLineSegment(sketch, "E88.bottom", {"start": v(270, 680) * mm, "end": v(250, 680) * mm});
            skLineSegment(sketch, "E88.top", {"start": v(270, 660) * mm, "end": v(250, 660) * mm});
            skLineSegment(sketch, "E88.left", {"start": v(270, 680) * mm, "end": v(270, 660) * mm});
            skLineSegment(sketch, "E88.right", {"start": v(250, 680) * mm, "end": v(250, 660) * mm});
            skLineSegment(sketch, "E89", {"start": v(-10, 680) * mm, "end": v(-220, 680) * mm});
            skLineSegment(sketch, "E90.bottom", {"start": v(-220, 680) * mm, "end": v(-240, 680) * mm});
            skLineSegment(sketch, "E90.top", {"start": v(-220, 660) * mm, "end": v(-240, 660) * mm});
            skLineSegment(sketch, "E90.left", {"start": v(-220, 680) * mm, "end": v(-220, 660) * mm});
            skLineSegment(sketch, "E90.right", {"start": v(-240, 680) * mm, "end": v(-240, 660) * mm});
            skLineSegment(sketch, "E91", {"start": v(-240, 680) * mm, "end": v(-470, 680) * mm});
            skLineSegment(sketch, "E92.bottom", {"start": v(-470, 680) * mm, "end": v(-490, 680) * mm});
            skLineSegment(sketch, "E92.top", {"start": v(-470, 660) * mm, "end": v(-490, 660) * mm});
            skLineSegment(sketch, "E92.left", {"start": v(-470, 680) * mm, "end": v(-470, 660) * mm});
            skLineSegment(sketch, "E92.right", {"start": v(-490, 680) * mm, "end": v(-490, 660) * mm});
            skLineSegment(sketch, "E93", {"start": v(730, 680) * mm, "end": v(730, 660) * mm});
            skSolve(sketch);
        }
        {
            var Q0;
            Q0 = qSketchRegion(id + "F22", true);
            extrude(context, id + "F23", {"entities" : qUnion([Q0]), "operationType" : NewBodyOperationType.REMOVE, "endBound" : BoundingType.UP_TO_NEXT, "oppositeDirection" : true, "depth" : 25 * mm, "offsetDistance" : 25 * mm});
        }
    });
